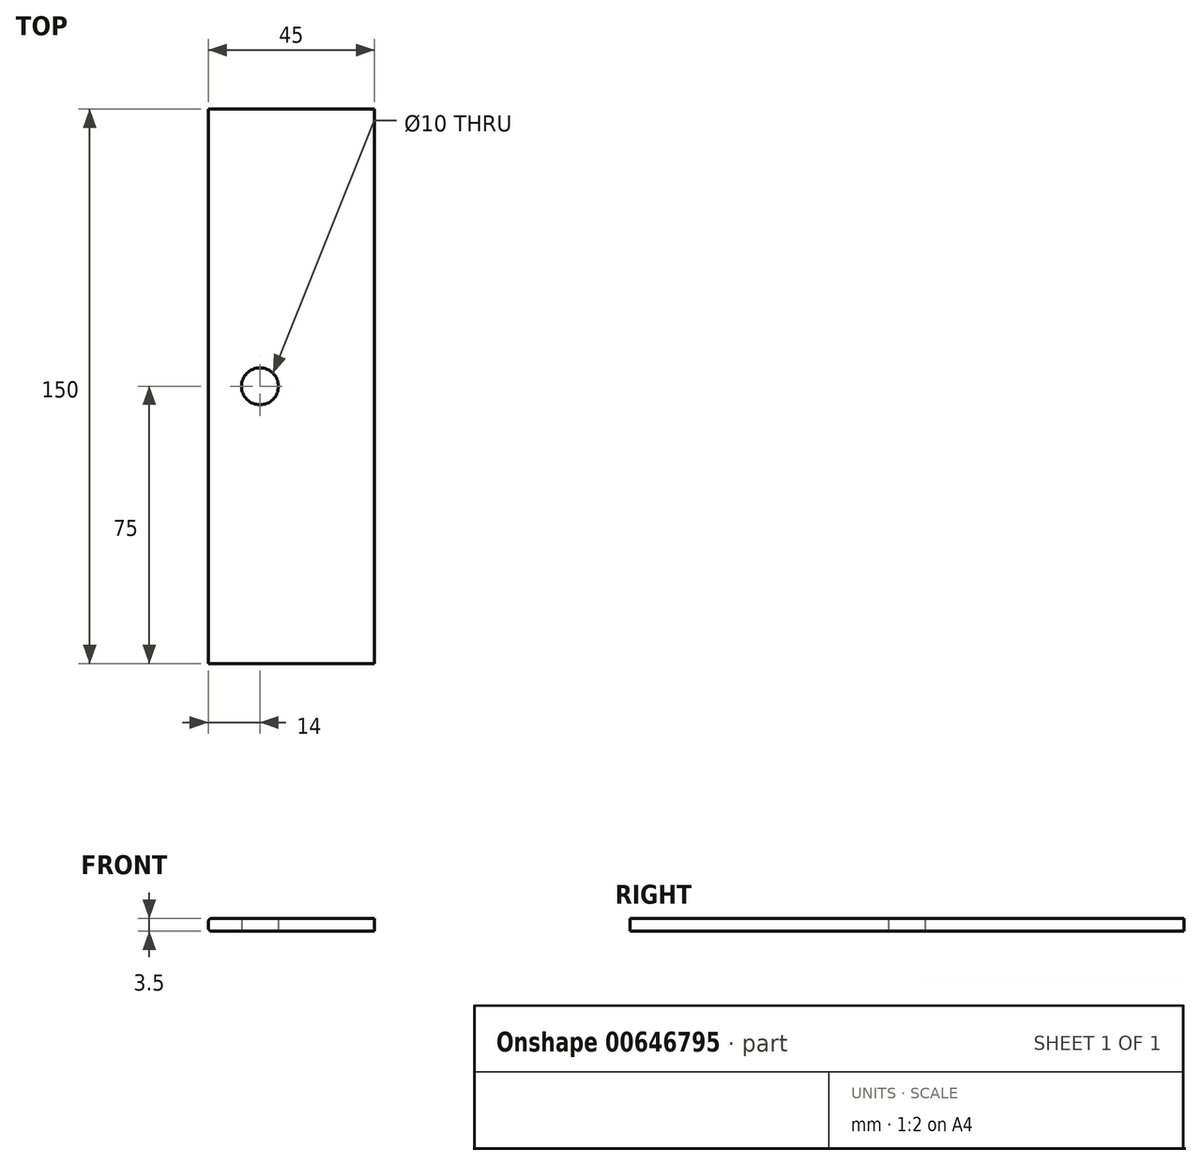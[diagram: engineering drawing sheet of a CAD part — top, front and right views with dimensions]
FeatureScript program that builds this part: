
annotation { "Feature Type Name" : "Feature", "Feature Type Description" : "" }
export const myFeature = defineFeature(function(context is Context, id is Id, definition is map)
    precondition{}
    {
        {
            var Q0;
            Q0=qCreatedBy(makeId("Front.planeOp"),FACE);
            var sketch = newSketch(context, id + "F0", { "sketchPlane" : qUnion([Q0])});
            skLineSegment(sketch, "E0.bottom", {"start": v(0, 0) * mm, "end": v(45, 0) * mm});
            skLineSegment(sketch, "E0.top", {"start": v(0, 3.5) * mm, "end": v(45, 3.5) * mm});
            skLineSegment(sketch, "E0.left", {"start": v(0, 0) * mm, "end": v(0, 3.5) * mm});
            skLineSegment(sketch, "E0.right", {"start": v(45, 0) * mm, "end": v(45, 3.5) * mm});
            skSolve(sketch);
        }
        {
            var Q0;
            Q0=makeQuery(id+"F0.imprint","IMPRINT",FACE,{"disambiguationData":[TD([[makeQuery(id+"F0.imprint","IMPRINT",EDGE,{"derivedFrom":sQuery(id+"F0.wireOp",EDGE,"E0.bottom")}),1.0]])]});
            extrude(context, id + "F1", {"entities" : qUnion([Q0]), "endBound" : BoundingType.SYMMETRIC, "depth" : 150 * mm, "offsetDistance" : 25 * mm});
        }
        {
            var Q0;
            Q0=qCreatedBy(makeId("Top.planeOp"),FACE);
            var sketch = newSketch(context, id + "F2", { "sketchPlane" : qUnion([Q0])});
            skCircle(sketch, "E1", {"center": v(14, 0) * mm, "radius": 5 * mm});
            skSolve(sketch);
        }
        {
            var Q0;
            Q0=qSketchRegion(id+"F2",true);
            extrude(context, id + "F3", {"entities" : qUnion([Q0]), "operationType" : NewBodyOperationType.REMOVE, "endBound" : BoundingType.UP_TO_NEXT, "depth" : 25 * mm, "offsetDistance" : 25 * mm});
        }
        {
            var Q0;
            Q0=makeQuery(id+"F1.opExtrude","SWEPT_EDGE",EDGE,{"disambiguationData":[OSD([sQuery(id+"F0.wireOp",EDGE,"E0.top"),sQuery(id+"F0.wireOp",EDGE,"E0.left")])]});
            var Q1;
            Q1=makeQuery(id+"F1.opExtrude","SWEPT_EDGE",EDGE,{"disambiguationData":[OSD([sQuery(id+"F0.wireOp",EDGE,"E0.bottom"),sQuery(id+"F0.wireOp",EDGE,"E0.left")])]});
            fillet(context, id + "F4", {"entities" : qUnion([Q0, Q1]), "radius" : 1 * mm, "tangentPropagation" : true, "allowEdgeOverflow" : false});
        }
    });
